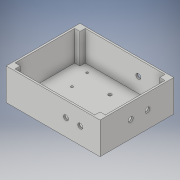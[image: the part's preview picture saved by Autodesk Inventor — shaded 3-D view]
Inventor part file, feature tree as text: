
AUTODESK INVENTOR PART (.ipt)
format: ipt  version: 2018 (Build 220112000, 112)  size: 189,952 bytes
history: native  units: in
note: dims shown in document units (in); Inventor stores cm internally (conversion verified against a paired STEP export)
features: extrude x7, sketch x7
ambient origin geometry x8: Origin, YZ Plane, XZ Plane, XY Plane, X Axis, Y Axis, Z Axis, Center Point
bodies: Solid1 (feature_tree)
feature tree (14):
  extrude  "Extrusion1"  Depth=3.701in
  extrude  "Extrusion2"  Depth=4.527in
  extrude  "Extrusion3"  Depth=0.354in
  extrude  "Extrusion6"  Depth=0.354in
  extrude  "Extrusion7"  Depth=1.5in TaperAngle=0.0deg
  extrude  "Extrusion8"  Depth=0.164in
  extrude  "Extrusion9"  Depth=3.543in
  sketch  "Sketch1"  dims[d0=4.705in d1=3.701in]
  sketch  "Sketch2"  dims[d2=0.089in d3=0.0in d4=4.527in]
  sketch  "Sketch3"  dims[d5=3.523in d6=0.354in]
  sketch  "Sketch7"  dims[d7=0.354in d10=0.354in]
  sketch  "Sketch8"  dims[d11=0.354in d14=1.5in d15=0.0in]
  sketch  "Sketch10"  dims[d18=0.164in d19=0.164in]
  sketch  "Sketch11"  dims[d20=0.0in d21=0.0in d47=3.543in d48=2.559in d58=0.112in d59=0.112in d60=0.112in d61=0.112in d62=2.598in d63=0.787in d64=0.118in d65=0.118in d66=0.118in d67=0.118in d68=0.0in d69=0.0in d72=1.0in d73=0.0in d78=0.0in d79=0.0in d80=0.227in d85=0.0in d86=0.0in d99=0.25in d112=0.25in d113=0.25in d118=0.25in d119=0.25in]
